# Revit family: ledwaterproof-p4_l1489-54w-840-em3_711000009900
name_source: partatom
category: Leuchten
revit_build: Autodesk Revit 2016 (Build: 20190508_0715(x64)
units: mm (PartAtom-declared; Revit-internal decimal feet)

## family parameters
Basisbauteil = Fläche
Beim Laden mit Abzugskörper schneiden = Nein
Bemaßung runder Anschluss = Durchmesser verwenden
Gemeinsam genutzt = Nein
Lichtquelle = Nein
Raumberechnungspunkt = Nein
Teiletyp = Normal

## types (1)
- LEDWaterproof-P4 L1489-54W-840-EM3 (1 x LED, 8100 lm, 4000)
    Approval mark = CE, ENEC
    Beschreibung = Powerful range of waterproof luminaires in specific "sealed for life" design. Quick installation thanks to its screwless endcap. Supplied with vandal-proof stainless steel ceiling and suspension clips.
    CIE Flux Codes = 42 72 90 90 103
    Color Rendering = 80
    Color Temperature = 4000
    Control Gear = Electronic ballast
    Frequency = 60 Hz
    Height = 75 mm
    Hersteller = OPPLE
    Lamp Light Flux = 8100 lm
    Lamp count = 1
    Lampe = 1 x LED
    Length = 1489 mm
    Luminous efficacy = 155 lm/W
    ModVariant = Nein
    Modell = 711000009900
    Mounting Place = Ceiling
    Mounting Type = Surface mounted, Pendant
    Number of Poles = 1
    OnlyDefault = Ja
    Power Factor = 1
    Product Name = LEDWaterproof-P4 L1489-54W-840-EM3
    Product group = Ceiling / wall-mounted luminaires
    ProductGroupID = 30
    Protection Class = Protection class II
    Protection Degree = IP 66
    RLX_Detail_Level = 1
    RlxData = <blob elided: 122601 chars, md5=f37c71bd>
    Scheinlast = 54 VA
    Socket = socket
    Standby Power = 0 W
    System Light Flux = 8380 lm
    System Power = 54 W
    Typenbild = web_wp_p4.jpg
    Typenkommentare = Product without accessories
    URL = http://relux.com
    VarID = ---
    Voltage = 230 V
    Voltage Range = 220-240 V
    Vorgabe-Ansicht = 1800 mm
    Weight = 0.00 kg
    Width = 63 mm

## geometry (parser evidence)
native form markers: Blend x4, Sweep x15
no freeform markers — native parametric forms only
